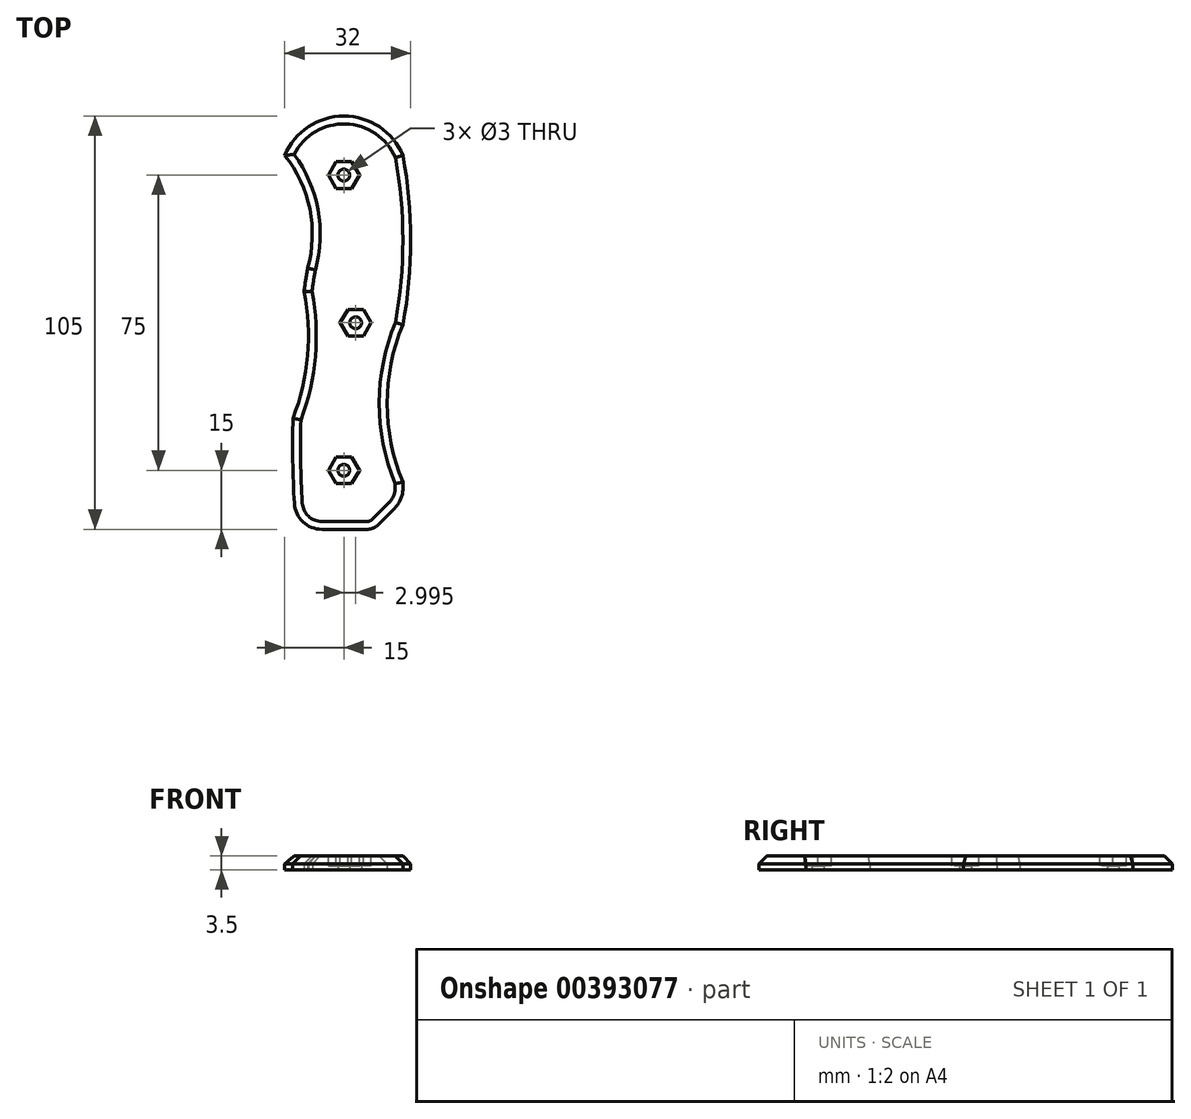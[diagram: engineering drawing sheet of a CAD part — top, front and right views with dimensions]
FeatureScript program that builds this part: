
annotation { "Feature Type Name" : "Feature", "Feature Type Description" : "" }
export const myFeature = defineFeature(function(context is Context, id is Id, definition is map)
    precondition{}
    {
        {
            var Q0;
            Q0=qCreatedBy(makeId("Top.planeOp"),FACE);
            var sketch = newSketch(context, id + "F0", { "sketchPlane" : qUnion([Q0])});
            skLineSegment(sketch, "E0.bottom", {"start": v(15.42, 23) * mm, "end": v(26.88, 23) * mm});
            skLineSegment(sketch, "E0.left", {"start": v(6, 0) * mm, "end": v(6, 118) * mm});
            skLineSegment(sketch, "E0.right", {"start": v(36, 10.36) * mm, "end": v(36, 118) * mm});
            skCircle(sketch, "E1", {"center": v(21, 113) * mm, "radius": 1.5 * mm});
            skPoint(sketch, "E1.centerSnap0", {"position": v(21, 128) * mm});
            skLineSegment(sketch, "E2", {"start": v(36, 78) * mm, "end": v(6, 78) * mm, "construction": true});
            skArc(sketch, "E3", {"start": v(36, 118) * mm, "mid": v(21, 128) * mm, "end": v(6, 118) * mm});
            skLineSegment(sketch, "E4", {"start": v(6, 118) * mm, "end": v(36, 118) * mm, "construction": true});
            skArc(sketch, "E5", {"start": v(11.81, 89.36) * mm, "mid": v(12.36, 104.38) * mm, "end": v(6, 118) * mm});
            skArc(sketch, "E6", {"start": v(11.81, 89.36) * mm, "mid": v(8.42, 59.58) * mm, "end": v(8.43, 29.6) * mm});
            skArc(sketch, "E7", {"start": v(8.08, 51.22) * mm, "mid": v(11.79, 67.12) * mm, "end": v(10.86, 83.43) * mm});
            skPoint(sketch, "E8.newPointA", {"position": v(11.81, 0) * mm});
            skPoint(sketch, "E8.newPointB", {"position": v(3, 23) * mm});
            skArc(sketch, "E8.filletArc", {"start": v(8.43, 29.6) * mm, "mid": v(10.61, 24.91) * mm, "end": v(15.42, 23) * mm});
            skPoint(sketch, "E9.visualSharp", {"position": v(36, 23) * mm});
            skLineSegment(sketch, "E10", {"start": v(29.7, 24.17) * mm, "end": v(33.95, 28.41) * mm});
            skArc(sketch, "E11.filletArc", {"start": v(26.88, 23) * mm, "mid": v(28.4, 23.3) * mm, "end": v(29.7, 24.17) * mm});
            skArc(sketch, "E12.filletArc", {"start": v(33.95, 28.41) * mm, "mid": v(35.47, 30.69) * mm, "end": v(36, 33.36) * mm});
            skArc(sketch, "E13", {"start": v(36, 75) * mm, "mid": v(32, 55) * mm, "end": v(36, 35) * mm});
            skArc(sketch, "E14", {"start": v(36, 75) * mm, "mid": v(38, 96.5) * mm, "end": v(36, 118) * mm});
            skLineSegment(sketch, "E15", {"start": v(21, 128) * mm, "end": v(21, 23) * mm, "construction": true});
            skPoint(sketch, "E15.endSnap0", {"position": v(21.15, 23) * mm});
            skLineSegment(sketch, "E16", {"start": v(36.1, 75.5) * mm, "end": v(11.9, 75.5) * mm, "construction": true});
            skPoint(sketch, "E16.endSnap0", {"position": v(21, 75.5) * mm});
            skCircle(sketch, "E17.MirrorC", {"center": v(21, 38) * mm, "radius": 1.5 * mm});
            skCircle(sketch, "E18", {"center": v(24, 75.5) * mm, "radius": 1.5 * mm});
            skSolve(sketch);
        }
        {
            var Q0;
            Q0=makeQuery(id+"F0.imprint","IMPRINT",FACE,{"disambiguationData":[TD([[makeQuery(id+"F0.imprint","IMPRINT",EDGE,{"derivedFrom":sQuery(id+"F0.wireOp",EDGE,"E1")}),-1.0]])]});
            var Q1;
            {var subQ0=sQuery(id+"F0.wireOp",EDGE,"E14");Q1=makeQuery(id+"F0.imprint","IMPRINT",FACE,{"disambiguationData":[TD([[makeQuery(id+"F0.imprint","IMPRINT",EDGE,{"derivedFrom":subQ0}),1.0]])]});}
            extrude(context, id + "F1", {"entities" : qUnion([Q0, Q1]), "depth" : 3.5 * mm});
        }
        {
            var Q0;
            Q0=makeQuery(id+"F1.opExtrude","CAP_FACE",FACE,{"disambiguationData":[OSD([sQuery(id+"F0.wireOp",EDGE,"E0.bottom"),sQuery(id+"F0.wireOp",EDGE,"E0.right"),sQuery(id+"F0.wireOp",EDGE,"E1"),sQuery(id+"F0.wireOp",EDGE,"E3"),sQuery(id+"F0.wireOp",EDGE,"E5"),sQuery(id+"F0.wireOp",EDGE,"E6"),sQuery(id+"F0.wireOp",EDGE,"E7"),sQuery(id+"F0.wireOp",EDGE,"E8.filletArc"),sQuery(id+"F0.wireOp",EDGE,"E10"),sQuery(id+"F0.wireOp",EDGE,"E11.filletArc"),sQuery(id+"F0.wireOp",EDGE,"E12.filletArc"),sQuery(id+"F0.wireOp",EDGE,"E13"),sQuery(id+"F0.wireOp",EDGE,"E14"),sQuery(id+"F0.wireOp",EDGE,"E17.MirrorC"),sQuery(id+"F0.wireOp",EDGE,"E18")])],"isStart":false});
            var sketch = newSketch(context, id + "F2", { "sketchPlane" : qUnion([Q0])});
            skCircle(sketch, "E19.cCircle", {"center": v(21, 113) * mm, "radius": 3.4 * mm, "construction": true});
            skLineSegment(sketch, "E19.0", {"start": v(24.93, 113) * mm, "end": v(22.96, 109.6) * mm});
            skLineSegment(sketch, "E19.1", {"start": v(22.96, 109.6) * mm, "end": v(19.04, 109.6) * mm});
            skLineSegment(sketch, "E19.2", {"start": v(19.04, 109.6) * mm, "end": v(17.07, 113) * mm});
            skLineSegment(sketch, "E19.3", {"start": v(17.07, 113) * mm, "end": v(19.04, 116.4) * mm});
            skLineSegment(sketch, "E19.4", {"start": v(19.04, 116.4) * mm, "end": v(22.96, 116.4) * mm});
            skLineSegment(sketch, "E19.5", {"start": v(22.96, 116.4) * mm, "end": v(24.93, 113) * mm});
            skPoint(sketch, "E19.0.midPoint", {"position": v(23.94, 111.3) * mm});
            skCircle(sketch, "E20.cCircle", {"center": v(24, 75.5) * mm, "radius": 3.4 * mm, "construction": true});
            skLineSegment(sketch, "E20.0", {"start": v(27.92, 75.5) * mm, "end": v(25.96, 72.1) * mm});
            skLineSegment(sketch, "E20.1", {"start": v(25.96, 72.1) * mm, "end": v(22.03, 72.1) * mm});
            skLineSegment(sketch, "E20.2", {"start": v(22.03, 72.1) * mm, "end": v(20.07, 75.5) * mm});
            skLineSegment(sketch, "E20.3", {"start": v(20.07, 75.5) * mm, "end": v(22.03, 78.9) * mm});
            skLineSegment(sketch, "E20.4", {"start": v(22.03, 78.9) * mm, "end": v(25.96, 78.9) * mm});
            skLineSegment(sketch, "E20.5", {"start": v(25.96, 78.9) * mm, "end": v(27.92, 75.5) * mm});
            skPoint(sketch, "E20.0.midPoint", {"position": v(26.94, 73.8) * mm});
            skCircle(sketch, "E21.cCircle", {"center": v(21, 38) * mm, "radius": 3.4 * mm, "construction": true});
            skLineSegment(sketch, "E21.0", {"start": v(24.93, 38) * mm, "end": v(22.96, 34.6) * mm});
            skLineSegment(sketch, "E21.1", {"start": v(22.96, 34.6) * mm, "end": v(19.04, 34.6) * mm});
            skLineSegment(sketch, "E21.2", {"start": v(19.04, 34.6) * mm, "end": v(17.07, 38) * mm});
            skLineSegment(sketch, "E21.3", {"start": v(17.07, 38) * mm, "end": v(19.04, 41.4) * mm});
            skLineSegment(sketch, "E21.4", {"start": v(19.04, 41.4) * mm, "end": v(22.96, 41.4) * mm});
            skLineSegment(sketch, "E21.5", {"start": v(22.96, 41.4) * mm, "end": v(24.93, 38) * mm});
            skPoint(sketch, "E21.0.midPoint", {"position": v(23.94, 36.3) * mm});
            skSolve(sketch);
        }
        {
            var Q0;
            Q0=makeQuery(id+"F1.opExtrude","CAP_EDGE",EDGE,{"disambiguationData":[OSD([sQuery(id+"F0.wireOp",EDGE,"E14")])],"isStart":false});
            var Q1;
            Q1=makeQuery(id+"F1.opExtrude","CAP_EDGE",EDGE,{"disambiguationData":[OSD([sQuery(id+"F0.wireOp",EDGE,"E13")])],"isStart":false});
            var Q2;
            Q2=makeQuery(id+"F1.opExtrude","CAP_EDGE",EDGE,{"disambiguationData":[OSD([sQuery(id+"F0.wireOp",EDGE,"E10")])],"isStart":false});
            var Q3;
            Q3=makeQuery(id+"F1.opExtrude","CAP_EDGE",EDGE,{"disambiguationData":[OSD([sQuery(id+"F0.wireOp",EDGE,"E7")])],"isStart":false});
            var Q4;
            Q4=makeQuery(id+"F1.opExtrude","CAP_EDGE",EDGE,{"disambiguationData":[OSD([sQuery(id+"F0.wireOp",EDGE,"E3")])],"isStart":false});
            var Q5;
            Q5=makeQuery(id+"F1.opExtrude","CAP_EDGE",EDGE,{"disambiguationData":[OSD([sQuery(id+"F0.wireOp",EDGE,"E5")])],"isStart":false});
            var Q6;
            {var subQ0=sQuery(id+"F0.wireOp",EDGE,"E6");Q6=makeQuery(id+"F1.opExtrude","CAP_EDGE",EDGE,{"disambiguationData":[OSD([subQ0]),TDD([makeQuery(id+"F0.imprint","IMPRINT",EDGE,{"disambiguationData":[TD([[makeQuery(id+"F0.imprint","INTERSECT",VERTEX,{"derivedFrom":[sQuery(id+"F0.wireOp",EDGE,"E5"),subQ0]}),-1.0]])],"derivedFrom":subQ0})])],"isStart":false});}
            chamfer(context, id + "F3", {"entities" : qUnion([Q0, Q1, Q2, Q3, Q4, Q5, Q6]), "width" : 2 * mm, "tangentPropagation" : true});
        }
        {
            var Q0;
            Q0=makeQuery(id+"F2.imprint","IMPRINT",FACE,{"disambiguationData":[TD([[makeQuery(id+"F2.imprint","IMPRINT",EDGE,{"derivedFrom":sQuery(id+"F2.wireOp",EDGE,"E19.0")}),-1.0]])]});
            var Q1;
            Q1=makeQuery(id+"F2.imprint","IMPRINT",FACE,{"disambiguationData":[TD([[makeQuery(id+"F2.imprint","IMPRINT",EDGE,{"derivedFrom":sQuery(id+"F2.wireOp",EDGE,"E20.0")}),-1.0]])]});
            var Q2;
            Q2=makeQuery(id+"F2.imprint","IMPRINT",FACE,{"disambiguationData":[TD([[makeQuery(id+"F2.imprint","IMPRINT",EDGE,{"derivedFrom":sQuery(id+"F2.wireOp",EDGE,"E21.0")}),-1.0]])]});
            extrude(context, id + "F4", {"entities" : qUnion([Q0, Q1, Q2]), "operationType" : NewBodyOperationType.REMOVE, "oppositeDirection" : true, "depth" : 2.5 * mm});
        }
    });
